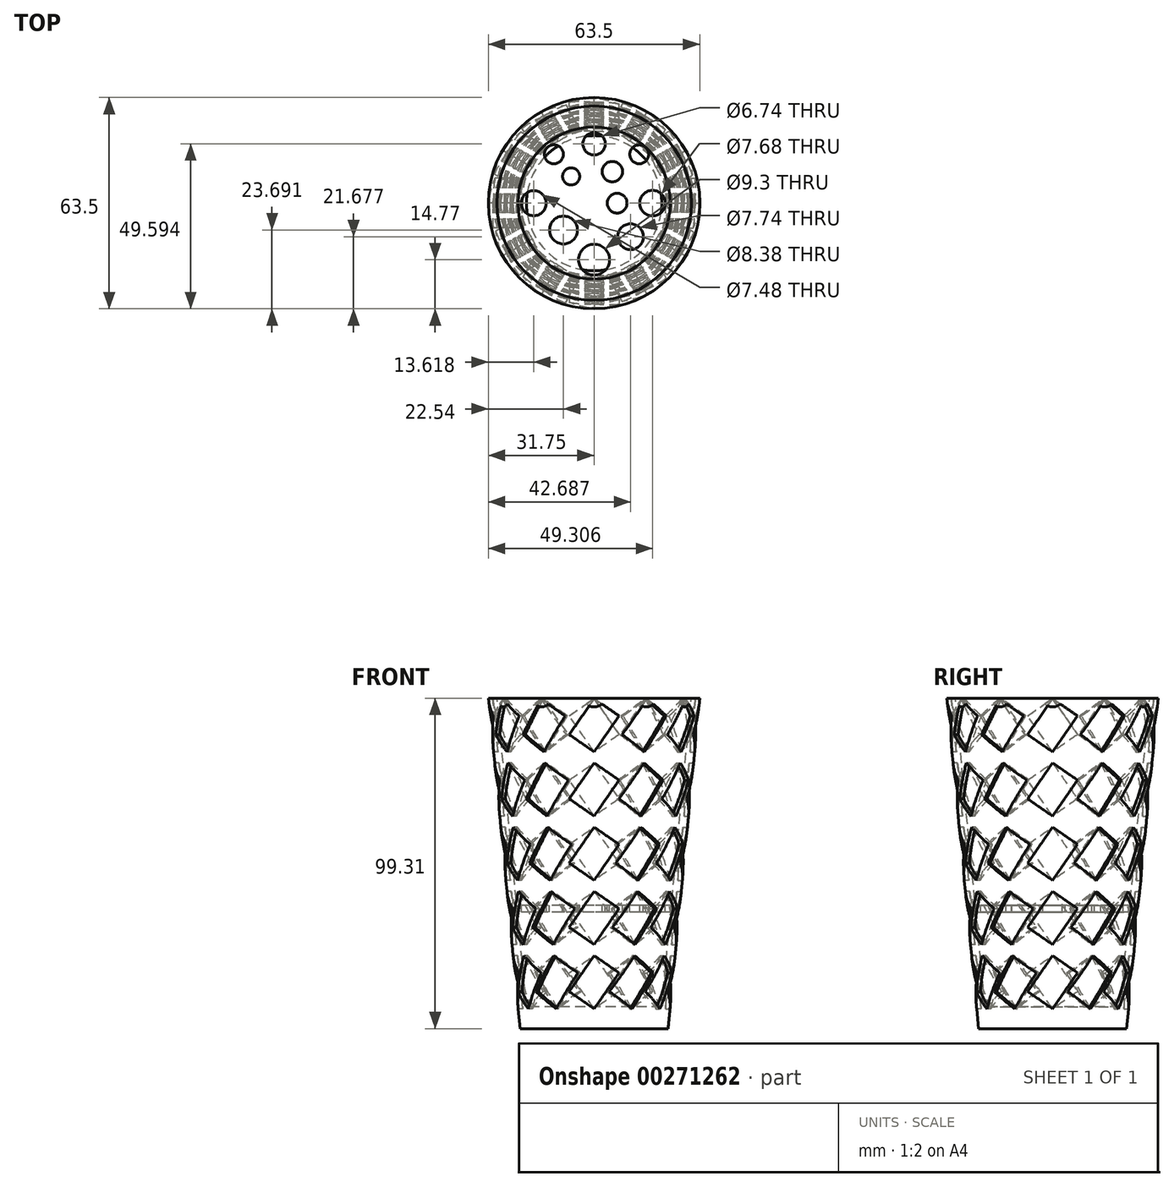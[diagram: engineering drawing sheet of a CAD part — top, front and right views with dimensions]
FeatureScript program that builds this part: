
annotation { "Feature Type Name" : "Feature", "Feature Type Description" : "" }
export const myFeature = defineFeature(function(context is Context, id is Id, definition is map)
    precondition{}
    {
        {
            var Q0;
            Q0=qCreatedBy(makeId("Top.planeOp"),FACE);
            cPlane(context, id + "F0", {"entities" : qUnion([Q0]), "cplaneType" : CPlaneType.OFFSET, "offset" : 50.8 * mm, "width" : 152.4 * mm, "height" : 152.4 * mm});
        }
        {
            var Q0;
            Q0=qCreatedBy(id+"F0.planeOp",FACE);
            var sketch = newSketch(context, id + "F1", { "sketchPlane" : qUnion([Q0])});
            skCircle(sketch, "E0", {"center": v(0, 0) * mm, "radius": 31.75 * mm});
            skSolve(sketch);
        }
        {
            var Q0;
            Q0=qCreatedBy(makeId("Top.planeOp"),FACE);
            cPlane(context, id + "F2", {"entities" : qUnion([Q0]), "cplaneType" : CPlaneType.OFFSET, "offset" : 48.5 * mm, "oppositeDirection" : true, "width" : 152.4 * mm, "height" : 152.4 * mm});
        }
        {
            var Q0;
            Q0=qCreatedBy(id+"F2.planeOp",FACE);
            var sketch = newSketch(context, id + "F3", { "sketchPlane" : qUnion([Q0])});
            skCircle(sketch, "E1", {"center": v(0, 0) * mm, "radius": 22.23 * mm});
            skSolve(sketch);
        }
        {
            var Q0;
            Q0=makeQuery(id+"F3.imprint","IMPRINT",FACE,{"disambiguationData":[TD([[makeQuery(id+"F3.imprint","IMPRINT",EDGE,{"derivedFrom":sQuery(id+"F3.wireOp",EDGE,"E1")}),1.0]])]});
            var Q1;
            Q1=makeQuery(id+"F1.imprint","IMPRINT",FACE,{"disambiguationData":[TD([[makeQuery(id+"F1.imprint","IMPRINT",EDGE,{"derivedFrom":sQuery(id+"F1.wireOp",EDGE,"E0")}),1.0]])]});
            loft(context, id + "F4", {"sheetProfilesArray" : [{ "sheetProfileEntities" : qUnion([Q0]) }, { "sheetProfileEntities" : qUnion([Q1]) }]});
        }
        {
            var Q0;
            Q0=qCreatedBy(makeId("Top.planeOp"),FACE);
            cPlane(context, id + "F5", {"entities" : qUnion([Q0]), "cplaneType" : CPlaneType.OFFSET, "offset" : 48.5 * mm, "oppositeDirection" : true, "width" : 152.4 * mm, "height" : 152.4 * mm});
        }
        {
            var Q0;
            Q0=qCreatedBy(id+"F5.planeOp",FACE);
            var sketch = newSketch(context, id + "F6", { "sketchPlane" : qUnion([Q0])});
            skCircle(sketch, "E2", {"center": v(0, 0) * mm, "radius": 22.23 * mm});
            skSolve(sketch);
        }
        {
            var Q0;
            Q0=makeQuery(id+"F4.opLoft","CAP_FACE",FACE,{"disambiguationData":[OSD([makeQuery(id+"F1.imprint","IMPRINT",FACE,{"disambiguationData":[TD([[makeQuery(id+"F1.imprint","IMPRINT",EDGE,{"derivedFrom":sQuery(id+"F1.wireOp",EDGE,"E0")}),1.0]])]})])],"isStart":true});
            var Q1;
            Q1=makeQuery(id+"F4.opLoft","CAP_FACE",FACE,{"disambiguationData":[OSD([makeQuery(id+"F3.imprint","IMPRINT",FACE,{"disambiguationData":[TD([[makeQuery(id+"F3.imprint","IMPRINT",EDGE,{"derivedFrom":sQuery(id+"F3.wireOp",EDGE,"E1")}),1.0]])]})])],"isStart":true});
            shell(context, id + "F7", {"entities" : qUnion([Q0, Q1]), "thickness" : 2.54 * mm});
        }
        {
            var Q0;
            Q0=makeQuery(id+"F6.imprint","IMPRINT",FACE,{"disambiguationData":[TD([[makeQuery(id+"F6.imprint","IMPRINT",EDGE,{"derivedFrom":sQuery(id+"F6.wireOp",EDGE,"E2")}),1.0]])]});
            extrude(context, id + "F8", {"entities" : qUnion([Q0]), "depth" : 6.35 * mm});
        }
        {
            var Q0;
            Q0=qCreatedBy(id+"F2.planeOp",FACE);
            cPlane(context, id + "F9", {"entities" : qUnion([Q0]), "cplaneType" : CPlaneType.OFFSET, "offset" : 35.05 * mm, "width" : 152.4 * mm, "height" : 152.4 * mm});
        }
        {
            var Q0;
            Q0=qCreatedBy(id+"F9.planeOp",FACE);
            var sketch = newSketch(context, id + "F10", { "sketchPlane" : qUnion([Q0])});
            skCircle(sketch, "E3", {"center": v(0, 0) * mm, "radius": 22.86 * mm});
            skSolve(sketch);
        }
        {
            var Q0;
            Q0=makeQuery(id+"F10.imprint","IMPRINT",FACE,{"disambiguationData":[TD([[makeQuery(id+"F10.imprint","IMPRINT",EDGE,{"derivedFrom":sQuery(id+"F10.wireOp",EDGE,"E3")}),1.0]])]});
            extrude(context, id + "F11", {"entities" : qUnion([Q0]), "depth" : 2.03 * mm});
        }
        {
            var Q0;
            Q0=makeQuery(id+"F11.opExtrude","CAP_FACE",FACE,{"disambiguationData":[OSD([sQuery(id+"F10.wireOp",EDGE,"E3")])],"isStart":false});
            var sketch = newSketch(context, id + "F12", { "sketchPlane" : qUnion([Q0])});
            skCircle(sketch, "E4", {"center": v(-12.09, 14.68) * mm, "radius": 2.85 * mm});
            skCircle(sketch, "E5", {"center": v(0, 17.84) * mm, "radius": 3.37 * mm});
            skCircle(sketch, "E6", {"center": v(13.53, 14.68) * mm, "radius": 2.83 * mm});
            skCircle(sketch, "E7", {"center": v(17.56, 0) * mm, "radius": 3.84 * mm});
            skCircle(sketch, "E8", {"center": v(0, -16.98) * mm, "radius": 4.65 * mm});
            skCircle(sketch, "E9", {"center": v(-18.13, 0) * mm, "radius": 3.74 * mm});
            skCircle(sketch, "E10", {"center": v(-9.2, -8.06) * mm, "radius": 4.2 * mm});
            skCircle(sketch, "E11", {"center": v(-6.9, 8.06) * mm, "radius": 2.57 * mm});
            skCircle(sketch, "E12", {"center": v(10.94, -10.07) * mm, "radius": 3.87 * mm});
            skCircle(sketch, "E13", {"center": v(5.47, 9.5) * mm, "radius": 3.06 * mm});
            skCircle(sketch, "E14", {"center": v(6.9, 0) * mm, "radius": 2.96 * mm});
            skSolve(sketch);
        }
        {
            var Q0;
            Q0 = qSketchRegion(id + "F12", true);
            extrude(context, id + "F13", {"entities" : qUnion([Q0]), "operationType" : NewBodyOperationType.REMOVE, "oppositeDirection" : true, "depth" : 4.06 * mm});
        }
        {
            var Q0;
            Q0=makeQuery(id+"F8.opExtrude","SWEPT_BODY",BODY,{"disambiguationData":[OSD([sQuery(id+"F6.wireOp",EDGE,"E2")])]});
            deleteBodies(context, id + "F14", {"entities" : qUnion([Q0])});
        }
        {
            var Q0;
            Q0=qCreatedBy(id+"F2.planeOp",FACE);
            var sketch = newSketch(context, id + "F15", { "sketchPlane" : qUnion([Q0])});
            skCircle(sketch, "E15", {"center": v(0, 0) * mm, "radius": 21.14 * mm});
            skSolve(sketch);
        }
        {
            var Q0;
            Q0=makeQuery(id+"F15.imprint","IMPRINT",FACE,{"disambiguationData":[TD([[makeQuery(id+"F15.imprint","IMPRINT",EDGE,{"derivedFrom":sQuery(id+"F15.wireOp",EDGE,"E15")}),1.0]])]});
            extrude(context, id + "F16", {"entities" : qUnion([Q0]), "operationType" : NewBodyOperationType.ADD, "depth" : 6.6 * mm});
        }
        {
            var Q0;
            Q0=makeQuery(id+"F16.boolean.opBoolean","MERGE",FACE,{"derivedFrom":[makeQuery(id+"F4.opLoft","CAP_FACE",FACE,{"disambiguationData":[OSD([makeQuery(id+"F3.imprint","IMPRINT",FACE,{"disambiguationData":[TD([[makeQuery(id+"F3.imprint","IMPRINT",EDGE,{"derivedFrom":sQuery(id+"F3.wireOp",EDGE,"E1")}),1.0]])]})])],"isStart":true}),makeQuery(id+"F16.opExtrude","CAP_FACE",FACE,{"disambiguationData":[OSD([sQuery(id+"F15.wireOp",EDGE,"E15")])],"isStart":true})]});
            var sketch = newSketch(context, id + "F17", { "sketchPlane" : qUnion([Q0])});
            skCircle(sketch, "E16", {"center": v(0, 0) * mm, "radius": 20.88 * mm});
            skSolve(sketch);
        }
        {
            var Q0;
            Q0=makeQuery(id+"F4.opLoft","CAP_FACE",FACE,{"disambiguationData":[OSD([makeQuery(id+"F1.imprint","IMPRINT",FACE,{"disambiguationData":[TD([[makeQuery(id+"F1.imprint","IMPRINT",EDGE,{"derivedFrom":sQuery(id+"F1.wireOp",EDGE,"E0")}),1.0]])]})])],"isStart":true});
            var sketch = newSketch(context, id + "F18", { "sketchPlane" : qUnion([Q0])});
            skCircle(sketch, "E17", {"center": v(0, 0) * mm, "radius": 30.42 * mm});
            skSolve(sketch);
        }
        {
            var Q0;
            Q0=makeQuery(id+"F18.imprint","IMPRINT",FACE,{"disambiguationData":[TD([[makeQuery(id+"F18.imprint","IMPRINT",EDGE,{"derivedFrom":sQuery(id+"F18.wireOp",EDGE,"E17")}),-1.0]])]});
            var Q1;
            Q1=sQuery(id+"F17.wireOp",EDGE,"E16");
            var Q2;
            Q2=sQuery(id+"F18.wireOp",EDGE,"E17");
            loft(context, id + "F19", {"bodyType" : ToolBodyType.SURFACE, "sheetProfilesArray" : [{ "sheetProfileEntities" : qUnion([Q0]) }], "wireProfilesArray" : [{ "wireProfileEntities" : qUnion([Q1]) }, { "wireProfileEntities" : qUnion([Q2]) }]});
        }
        {
            var Q0;
            Q0=qCreatedBy(makeId("Right.planeOp"),FACE);
            cPlane(context, id + "F20", {"entities" : qUnion([Q0]), "cplaneType" : CPlaneType.OFFSET, "offset" : 31.5 * mm, "width" : 152.4 * mm, "height" : 152.4 * mm});
        }
        {
            var Q0;
            Q0=qCreatedBy(id+"F20.planeOp",FACE);
            var sketch = newSketch(context, id + "F21", { "sketchPlane" : qUnion([Q0])});
            skLineSegment(sketch, "E18", {"start": v(0, 50.65) * mm, "end": v(7.48, 45.47) * mm});
            skLineSegment(sketch, "E19", {"start": v(7.48, 45.47) * mm, "end": v(0, 34.66) * mm});
            skLineSegment(sketch, "E20", {"start": v(0, 34.66) * mm, "end": v(-7.48, 39.85) * mm});
            skLineSegment(sketch, "E21", {"start": v(-7.48, 39.85) * mm, "end": v(0, 50.65) * mm});
            skLineSegment(sketch, "E22.0.1.0", {"start": v(0, 31.35) * mm, "end": v(7.48, 26.17) * mm});
            skLineSegment(sketch, "E22.0.1.1", {"start": v(7.48, 26.17) * mm, "end": v(0, 15.36) * mm});
            skLineSegment(sketch, "E22.0.1.2", {"start": v(0, 15.36) * mm, "end": v(-7.48, 20.54) * mm});
            skLineSegment(sketch, "E22.0.1.3", {"start": v(-7.48, 20.54) * mm, "end": v(0, 31.35) * mm});
            skLineSegment(sketch, "E22.0.2.0", {"start": v(0, 12.05) * mm, "end": v(7.48, 6.87) * mm});
            skLineSegment(sketch, "E22.0.2.1", {"start": v(7.48, 6.87) * mm, "end": v(0, -3.94) * mm});
            skLineSegment(sketch, "E22.0.2.2", {"start": v(0, -3.94) * mm, "end": v(-7.48, 1.24) * mm});
            skLineSegment(sketch, "E22.0.2.3", {"start": v(-7.48, 1.24) * mm, "end": v(0, 12.05) * mm});
            skLineSegment(sketch, "E22.0.3.0", {"start": v(0, -7.26) * mm, "end": v(7.48, -12.44) * mm});
            skLineSegment(sketch, "E22.0.3.1", {"start": v(7.48, -12.44) * mm, "end": v(0, -23.25) * mm});
            skLineSegment(sketch, "E22.0.3.2", {"start": v(0, -23.25) * mm, "end": v(-7.48, -18.07) * mm});
            skLineSegment(sketch, "E22.0.3.3", {"start": v(-7.48, -18.07) * mm, "end": v(0, -7.26) * mm});
            skLineSegment(sketch, "E22.0.4.0", {"start": v(0, -26.56) * mm, "end": v(7.48, -31.74) * mm});
            skLineSegment(sketch, "E22.0.4.1", {"start": v(7.48, -31.74) * mm, "end": v(0, -42.55) * mm});
            skLineSegment(sketch, "E22.0.4.2", {"start": v(0, -42.55) * mm, "end": v(-7.48, -37.37) * mm});
            skLineSegment(sketch, "E22.0.4.3", {"start": v(-7.48, -37.37) * mm, "end": v(0, -26.56) * mm});
            skLineSegment(sketch, "E22.direction1", {"start": v(-7.48, 39.85) * mm, "end": v(17.92, 39.85) * mm, "construction": true});
            skLineSegment(sketch, "E22.direction2", {"start": v(-7.48, 39.85) * mm, "end": v(-7.48, 20.54) * mm, "construction": true});
            skSolve(sketch);
        }
        {
            var Q0;
            Q0 = qSketchRegion(id + "F21", true);
            var Q1;
            Q1=makeQuery(id+"F19.opLoft","SWEPT_BODY",BODY,{"disambiguationData":[OSD([sQuery(id+"F17.wireOp",EDGE,"E16"),sQuery(id+"F18.wireOp",EDGE,"E17")])]});
            extrude(context, id + "F22", {"entities" : qUnion([Q0]), "endBound" : BoundingType.UP_TO_BODY, "oppositeDirection" : true, "endBoundEntityBody" : qUnion([Q1]), "depth" : 2.54 * mm});
        }
        {
            var Q0;
            Q0=qCreatedBy(makeId("Front.planeOp"),FACE);
            var sketch = newSketch(context, id + "F23", { "sketchPlane" : qUnion([Q0])});
            skLineSegment(sketch, "E23", {"start": v(0, -61.6) * mm, "end": v(0, 66.06) * mm, "construction": true});
            skSolve(sketch);
        }
        {
            var Q0;
            Q0=makeQuery(id+"F22.opExtrude","SWEPT_BODY",BODY,{"disambiguationData":[OSD([sQuery(id+"F21.wireOp",EDGE,"E18"),sQuery(id+"F21.wireOp",EDGE,"E19"),sQuery(id+"F21.wireOp",EDGE,"E20"),sQuery(id+"F21.wireOp",EDGE,"E21")])]});
            var Q1;
            Q1=makeQuery(id+"F22.opExtrude","SWEPT_BODY",BODY,{"disambiguationData":[OSD([sQuery(id+"F21.wireOp",EDGE,"E22.0.1.0"),sQuery(id+"F21.wireOp",EDGE,"E22.0.1.1"),sQuery(id+"F21.wireOp",EDGE,"E22.0.1.2"),sQuery(id+"F21.wireOp",EDGE,"E22.0.1.3")])]});
            var Q2;
            Q2=makeQuery(id+"F22.opExtrude","SWEPT_BODY",BODY,{"disambiguationData":[OSD([sQuery(id+"F21.wireOp",EDGE,"E22.0.2.0"),sQuery(id+"F21.wireOp",EDGE,"E22.0.2.1"),sQuery(id+"F21.wireOp",EDGE,"E22.0.2.2"),sQuery(id+"F21.wireOp",EDGE,"E22.0.2.3")])]});
            var Q3;
            Q3=makeQuery(id+"F22.opExtrude","SWEPT_BODY",BODY,{"disambiguationData":[OSD([sQuery(id+"F21.wireOp",EDGE,"E22.0.3.0"),sQuery(id+"F21.wireOp",EDGE,"E22.0.3.1"),sQuery(id+"F21.wireOp",EDGE,"E22.0.3.2"),sQuery(id+"F21.wireOp",EDGE,"E22.0.3.3")])]});
            var Q4;
            Q4=makeQuery(id+"F22.opExtrude","SWEPT_BODY",BODY,{"disambiguationData":[OSD([sQuery(id+"F21.wireOp",EDGE,"E22.0.4.0"),sQuery(id+"F21.wireOp",EDGE,"E22.0.4.1"),sQuery(id+"F21.wireOp",EDGE,"E22.0.4.2"),sQuery(id+"F21.wireOp",EDGE,"E22.0.4.3")])]});
            var Q5;
            Q5=sQuery(id+"F23.wireOp",EDGE,"E23");
            circularPattern(context, id + "F24", {"entities" : qUnion([Q0, Q1, Q2, Q3, Q4]), "axis" : qUnion([Q5]), "angle" : 360 * degree, "instanceCount" : 12, "equalSpace" : true});
        }
        {
            var Q0;
            Q0=makeQuery(id+"F24.opPattern","COPY",BODY,{"derivedFrom":makeQuery(id+"F22.opExtrude","SWEPT_BODY",BODY,{"disambiguationData":[OSD([sQuery(id+"F21.wireOp",EDGE,"E22.0.4.0"),sQuery(id+"F21.wireOp",EDGE,"E22.0.4.1"),sQuery(id+"F21.wireOp",EDGE,"E22.0.4.2"),sQuery(id+"F21.wireOp",EDGE,"E22.0.4.3")])]}),"instanceName":"11"});
            var Q1;
            Q1=makeQuery(id+"F22.opExtrude","SWEPT_BODY",BODY,{"disambiguationData":[OSD([sQuery(id+"F21.wireOp",EDGE,"E18"),sQuery(id+"F21.wireOp",EDGE,"E19"),sQuery(id+"F21.wireOp",EDGE,"E20"),sQuery(id+"F21.wireOp",EDGE,"E21")])]});
            var Q2;
            Q2=makeQuery(id+"F22.opExtrude","SWEPT_BODY",BODY,{"disambiguationData":[OSD([sQuery(id+"F21.wireOp",EDGE,"E22.0.1.0"),sQuery(id+"F21.wireOp",EDGE,"E22.0.1.1"),sQuery(id+"F21.wireOp",EDGE,"E22.0.1.2"),sQuery(id+"F21.wireOp",EDGE,"E22.0.1.3")])]});
            var Q3;
            Q3=makeQuery(id+"F22.opExtrude","SWEPT_BODY",BODY,{"disambiguationData":[OSD([sQuery(id+"F21.wireOp",EDGE,"E22.0.2.0"),sQuery(id+"F21.wireOp",EDGE,"E22.0.2.1"),sQuery(id+"F21.wireOp",EDGE,"E22.0.2.2"),sQuery(id+"F21.wireOp",EDGE,"E22.0.2.3")])]});
            var Q4;
            Q4=makeQuery(id+"F22.opExtrude","SWEPT_BODY",BODY,{"disambiguationData":[OSD([sQuery(id+"F21.wireOp",EDGE,"E22.0.3.0"),sQuery(id+"F21.wireOp",EDGE,"E22.0.3.1"),sQuery(id+"F21.wireOp",EDGE,"E22.0.3.2"),sQuery(id+"F21.wireOp",EDGE,"E22.0.3.3")])]});
            var Q5;
            Q5=makeQuery(id+"F22.opExtrude","SWEPT_BODY",BODY,{"disambiguationData":[OSD([sQuery(id+"F21.wireOp",EDGE,"E22.0.4.0"),sQuery(id+"F21.wireOp",EDGE,"E22.0.4.1"),sQuery(id+"F21.wireOp",EDGE,"E22.0.4.2"),sQuery(id+"F21.wireOp",EDGE,"E22.0.4.3")])]});
            var Q6;
            Q6=makeQuery(id+"F24.opPattern","COPY",BODY,{"derivedFrom":makeQuery(id+"F22.opExtrude","SWEPT_BODY",BODY,{"disambiguationData":[OSD([sQuery(id+"F21.wireOp",EDGE,"E18"),sQuery(id+"F21.wireOp",EDGE,"E19"),sQuery(id+"F21.wireOp",EDGE,"E20"),sQuery(id+"F21.wireOp",EDGE,"E21")])]}),"instanceName":"1"});
            var Q7;
            Q7=makeQuery(id+"F24.opPattern","COPY",BODY,{"derivedFrom":makeQuery(id+"F22.opExtrude","SWEPT_BODY",BODY,{"disambiguationData":[OSD([sQuery(id+"F21.wireOp",EDGE,"E22.0.1.0"),sQuery(id+"F21.wireOp",EDGE,"E22.0.1.1"),sQuery(id+"F21.wireOp",EDGE,"E22.0.1.2"),sQuery(id+"F21.wireOp",EDGE,"E22.0.1.3")])]}),"instanceName":"1"});
            var Q8;
            Q8=makeQuery(id+"F24.opPattern","COPY",BODY,{"derivedFrom":makeQuery(id+"F22.opExtrude","SWEPT_BODY",BODY,{"disambiguationData":[OSD([sQuery(id+"F21.wireOp",EDGE,"E22.0.2.0"),sQuery(id+"F21.wireOp",EDGE,"E22.0.2.1"),sQuery(id+"F21.wireOp",EDGE,"E22.0.2.2"),sQuery(id+"F21.wireOp",EDGE,"E22.0.2.3")])]}),"instanceName":"1"});
            var Q9;
            Q9=makeQuery(id+"F24.opPattern","COPY",BODY,{"derivedFrom":makeQuery(id+"F22.opExtrude","SWEPT_BODY",BODY,{"disambiguationData":[OSD([sQuery(id+"F21.wireOp",EDGE,"E22.0.3.0"),sQuery(id+"F21.wireOp",EDGE,"E22.0.3.1"),sQuery(id+"F21.wireOp",EDGE,"E22.0.3.2"),sQuery(id+"F21.wireOp",EDGE,"E22.0.3.3")])]}),"instanceName":"1"});
            var Q10;
            Q10=makeQuery(id+"F24.opPattern","COPY",BODY,{"derivedFrom":makeQuery(id+"F22.opExtrude","SWEPT_BODY",BODY,{"disambiguationData":[OSD([sQuery(id+"F21.wireOp",EDGE,"E22.0.4.0"),sQuery(id+"F21.wireOp",EDGE,"E22.0.4.1"),sQuery(id+"F21.wireOp",EDGE,"E22.0.4.2"),sQuery(id+"F21.wireOp",EDGE,"E22.0.4.3")])]}),"instanceName":"1"});
            var Q11;
            Q11=makeQuery(id+"F24.opPattern","COPY",BODY,{"derivedFrom":makeQuery(id+"F22.opExtrude","SWEPT_BODY",BODY,{"disambiguationData":[OSD([sQuery(id+"F21.wireOp",EDGE,"E18"),sQuery(id+"F21.wireOp",EDGE,"E19"),sQuery(id+"F21.wireOp",EDGE,"E20"),sQuery(id+"F21.wireOp",EDGE,"E21")])]}),"instanceName":"2"});
            var Q12;
            Q12=makeQuery(id+"F24.opPattern","COPY",BODY,{"derivedFrom":makeQuery(id+"F22.opExtrude","SWEPT_BODY",BODY,{"disambiguationData":[OSD([sQuery(id+"F21.wireOp",EDGE,"E22.0.1.0"),sQuery(id+"F21.wireOp",EDGE,"E22.0.1.1"),sQuery(id+"F21.wireOp",EDGE,"E22.0.1.2"),sQuery(id+"F21.wireOp",EDGE,"E22.0.1.3")])]}),"instanceName":"2"});
            var Q13;
            Q13=makeQuery(id+"F24.opPattern","COPY",BODY,{"derivedFrom":makeQuery(id+"F22.opExtrude","SWEPT_BODY",BODY,{"disambiguationData":[OSD([sQuery(id+"F21.wireOp",EDGE,"E22.0.2.0"),sQuery(id+"F21.wireOp",EDGE,"E22.0.2.1"),sQuery(id+"F21.wireOp",EDGE,"E22.0.2.2"),sQuery(id+"F21.wireOp",EDGE,"E22.0.2.3")])]}),"instanceName":"2"});
            var Q14;
            Q14=makeQuery(id+"F24.opPattern","COPY",BODY,{"derivedFrom":makeQuery(id+"F22.opExtrude","SWEPT_BODY",BODY,{"disambiguationData":[OSD([sQuery(id+"F21.wireOp",EDGE,"E22.0.3.0"),sQuery(id+"F21.wireOp",EDGE,"E22.0.3.1"),sQuery(id+"F21.wireOp",EDGE,"E22.0.3.2"),sQuery(id+"F21.wireOp",EDGE,"E22.0.3.3")])]}),"instanceName":"2"});
            var Q15;
            Q15=makeQuery(id+"F24.opPattern","COPY",BODY,{"derivedFrom":makeQuery(id+"F22.opExtrude","SWEPT_BODY",BODY,{"disambiguationData":[OSD([sQuery(id+"F21.wireOp",EDGE,"E22.0.4.0"),sQuery(id+"F21.wireOp",EDGE,"E22.0.4.1"),sQuery(id+"F21.wireOp",EDGE,"E22.0.4.2"),sQuery(id+"F21.wireOp",EDGE,"E22.0.4.3")])]}),"instanceName":"2"});
            var Q16;
            Q16=makeQuery(id+"F24.opPattern","COPY",BODY,{"derivedFrom":makeQuery(id+"F22.opExtrude","SWEPT_BODY",BODY,{"disambiguationData":[OSD([sQuery(id+"F21.wireOp",EDGE,"E18"),sQuery(id+"F21.wireOp",EDGE,"E19"),sQuery(id+"F21.wireOp",EDGE,"E20"),sQuery(id+"F21.wireOp",EDGE,"E21")])]}),"instanceName":"3"});
            var Q17;
            Q17=makeQuery(id+"F24.opPattern","COPY",BODY,{"derivedFrom":makeQuery(id+"F22.opExtrude","SWEPT_BODY",BODY,{"disambiguationData":[OSD([sQuery(id+"F21.wireOp",EDGE,"E22.0.1.0"),sQuery(id+"F21.wireOp",EDGE,"E22.0.1.1"),sQuery(id+"F21.wireOp",EDGE,"E22.0.1.2"),sQuery(id+"F21.wireOp",EDGE,"E22.0.1.3")])]}),"instanceName":"3"});
            var Q18;
            Q18=makeQuery(id+"F24.opPattern","COPY",BODY,{"derivedFrom":makeQuery(id+"F22.opExtrude","SWEPT_BODY",BODY,{"disambiguationData":[OSD([sQuery(id+"F21.wireOp",EDGE,"E22.0.2.0"),sQuery(id+"F21.wireOp",EDGE,"E22.0.2.1"),sQuery(id+"F21.wireOp",EDGE,"E22.0.2.2"),sQuery(id+"F21.wireOp",EDGE,"E22.0.2.3")])]}),"instanceName":"3"});
            var Q19;
            Q19=makeQuery(id+"F24.opPattern","COPY",BODY,{"derivedFrom":makeQuery(id+"F22.opExtrude","SWEPT_BODY",BODY,{"disambiguationData":[OSD([sQuery(id+"F21.wireOp",EDGE,"E22.0.3.0"),sQuery(id+"F21.wireOp",EDGE,"E22.0.3.1"),sQuery(id+"F21.wireOp",EDGE,"E22.0.3.2"),sQuery(id+"F21.wireOp",EDGE,"E22.0.3.3")])]}),"instanceName":"3"});
            var Q20;
            Q20=makeQuery(id+"F24.opPattern","COPY",BODY,{"derivedFrom":makeQuery(id+"F22.opExtrude","SWEPT_BODY",BODY,{"disambiguationData":[OSD([sQuery(id+"F21.wireOp",EDGE,"E22.0.4.0"),sQuery(id+"F21.wireOp",EDGE,"E22.0.4.1"),sQuery(id+"F21.wireOp",EDGE,"E22.0.4.2"),sQuery(id+"F21.wireOp",EDGE,"E22.0.4.3")])]}),"instanceName":"3"});
            var Q21;
            Q21=makeQuery(id+"F24.opPattern","COPY",BODY,{"derivedFrom":makeQuery(id+"F22.opExtrude","SWEPT_BODY",BODY,{"disambiguationData":[OSD([sQuery(id+"F21.wireOp",EDGE,"E18"),sQuery(id+"F21.wireOp",EDGE,"E19"),sQuery(id+"F21.wireOp",EDGE,"E20"),sQuery(id+"F21.wireOp",EDGE,"E21")])]}),"instanceName":"4"});
            var Q22;
            Q22=makeQuery(id+"F24.opPattern","COPY",BODY,{"derivedFrom":makeQuery(id+"F22.opExtrude","SWEPT_BODY",BODY,{"disambiguationData":[OSD([sQuery(id+"F21.wireOp",EDGE,"E22.0.1.0"),sQuery(id+"F21.wireOp",EDGE,"E22.0.1.1"),sQuery(id+"F21.wireOp",EDGE,"E22.0.1.2"),sQuery(id+"F21.wireOp",EDGE,"E22.0.1.3")])]}),"instanceName":"4"});
            var Q23;
            Q23=makeQuery(id+"F24.opPattern","COPY",BODY,{"derivedFrom":makeQuery(id+"F22.opExtrude","SWEPT_BODY",BODY,{"disambiguationData":[OSD([sQuery(id+"F21.wireOp",EDGE,"E22.0.2.0"),sQuery(id+"F21.wireOp",EDGE,"E22.0.2.1"),sQuery(id+"F21.wireOp",EDGE,"E22.0.2.2"),sQuery(id+"F21.wireOp",EDGE,"E22.0.2.3")])]}),"instanceName":"4"});
            var Q24;
            Q24=makeQuery(id+"F24.opPattern","COPY",BODY,{"derivedFrom":makeQuery(id+"F22.opExtrude","SWEPT_BODY",BODY,{"disambiguationData":[OSD([sQuery(id+"F21.wireOp",EDGE,"E22.0.3.0"),sQuery(id+"F21.wireOp",EDGE,"E22.0.3.1"),sQuery(id+"F21.wireOp",EDGE,"E22.0.3.2"),sQuery(id+"F21.wireOp",EDGE,"E22.0.3.3")])]}),"instanceName":"4"});
            var Q25;
            Q25=makeQuery(id+"F24.opPattern","COPY",BODY,{"derivedFrom":makeQuery(id+"F22.opExtrude","SWEPT_BODY",BODY,{"disambiguationData":[OSD([sQuery(id+"F21.wireOp",EDGE,"E22.0.4.0"),sQuery(id+"F21.wireOp",EDGE,"E22.0.4.1"),sQuery(id+"F21.wireOp",EDGE,"E22.0.4.2"),sQuery(id+"F21.wireOp",EDGE,"E22.0.4.3")])]}),"instanceName":"4"});
            var Q26;
            Q26=makeQuery(id+"F24.opPattern","COPY",BODY,{"derivedFrom":makeQuery(id+"F22.opExtrude","SWEPT_BODY",BODY,{"disambiguationData":[OSD([sQuery(id+"F21.wireOp",EDGE,"E18"),sQuery(id+"F21.wireOp",EDGE,"E19"),sQuery(id+"F21.wireOp",EDGE,"E20"),sQuery(id+"F21.wireOp",EDGE,"E21")])]}),"instanceName":"5"});
            var Q27;
            Q27=makeQuery(id+"F24.opPattern","COPY",BODY,{"derivedFrom":makeQuery(id+"F22.opExtrude","SWEPT_BODY",BODY,{"disambiguationData":[OSD([sQuery(id+"F21.wireOp",EDGE,"E22.0.1.0"),sQuery(id+"F21.wireOp",EDGE,"E22.0.1.1"),sQuery(id+"F21.wireOp",EDGE,"E22.0.1.2"),sQuery(id+"F21.wireOp",EDGE,"E22.0.1.3")])]}),"instanceName":"5"});
            var Q28;
            Q28=makeQuery(id+"F24.opPattern","COPY",BODY,{"derivedFrom":makeQuery(id+"F22.opExtrude","SWEPT_BODY",BODY,{"disambiguationData":[OSD([sQuery(id+"F21.wireOp",EDGE,"E22.0.2.0"),sQuery(id+"F21.wireOp",EDGE,"E22.0.2.1"),sQuery(id+"F21.wireOp",EDGE,"E22.0.2.2"),sQuery(id+"F21.wireOp",EDGE,"E22.0.2.3")])]}),"instanceName":"5"});
            var Q29;
            Q29=makeQuery(id+"F24.opPattern","COPY",BODY,{"derivedFrom":makeQuery(id+"F22.opExtrude","SWEPT_BODY",BODY,{"disambiguationData":[OSD([sQuery(id+"F21.wireOp",EDGE,"E22.0.3.0"),sQuery(id+"F21.wireOp",EDGE,"E22.0.3.1"),sQuery(id+"F21.wireOp",EDGE,"E22.0.3.2"),sQuery(id+"F21.wireOp",EDGE,"E22.0.3.3")])]}),"instanceName":"5"});
            var Q30;
            Q30=makeQuery(id+"F24.opPattern","COPY",BODY,{"derivedFrom":makeQuery(id+"F22.opExtrude","SWEPT_BODY",BODY,{"disambiguationData":[OSD([sQuery(id+"F21.wireOp",EDGE,"E22.0.4.0"),sQuery(id+"F21.wireOp",EDGE,"E22.0.4.1"),sQuery(id+"F21.wireOp",EDGE,"E22.0.4.2"),sQuery(id+"F21.wireOp",EDGE,"E22.0.4.3")])]}),"instanceName":"5"});
            var Q31;
            Q31=makeQuery(id+"F24.opPattern","COPY",BODY,{"derivedFrom":makeQuery(id+"F22.opExtrude","SWEPT_BODY",BODY,{"disambiguationData":[OSD([sQuery(id+"F21.wireOp",EDGE,"E18"),sQuery(id+"F21.wireOp",EDGE,"E19"),sQuery(id+"F21.wireOp",EDGE,"E20"),sQuery(id+"F21.wireOp",EDGE,"E21")])]}),"instanceName":"6"});
            var Q32;
            Q32=makeQuery(id+"F24.opPattern","COPY",BODY,{"derivedFrom":makeQuery(id+"F22.opExtrude","SWEPT_BODY",BODY,{"disambiguationData":[OSD([sQuery(id+"F21.wireOp",EDGE,"E22.0.1.0"),sQuery(id+"F21.wireOp",EDGE,"E22.0.1.1"),sQuery(id+"F21.wireOp",EDGE,"E22.0.1.2"),sQuery(id+"F21.wireOp",EDGE,"E22.0.1.3")])]}),"instanceName":"6"});
            var Q33;
            Q33=makeQuery(id+"F24.opPattern","COPY",BODY,{"derivedFrom":makeQuery(id+"F22.opExtrude","SWEPT_BODY",BODY,{"disambiguationData":[OSD([sQuery(id+"F21.wireOp",EDGE,"E22.0.2.0"),sQuery(id+"F21.wireOp",EDGE,"E22.0.2.1"),sQuery(id+"F21.wireOp",EDGE,"E22.0.2.2"),sQuery(id+"F21.wireOp",EDGE,"E22.0.2.3")])]}),"instanceName":"6"});
            var Q34;
            Q34=makeQuery(id+"F24.opPattern","COPY",BODY,{"derivedFrom":makeQuery(id+"F22.opExtrude","SWEPT_BODY",BODY,{"disambiguationData":[OSD([sQuery(id+"F21.wireOp",EDGE,"E22.0.3.0"),sQuery(id+"F21.wireOp",EDGE,"E22.0.3.1"),sQuery(id+"F21.wireOp",EDGE,"E22.0.3.2"),sQuery(id+"F21.wireOp",EDGE,"E22.0.3.3")])]}),"instanceName":"6"});
            var Q35;
            Q35=makeQuery(id+"F24.opPattern","COPY",BODY,{"derivedFrom":makeQuery(id+"F22.opExtrude","SWEPT_BODY",BODY,{"disambiguationData":[OSD([sQuery(id+"F21.wireOp",EDGE,"E22.0.4.0"),sQuery(id+"F21.wireOp",EDGE,"E22.0.4.1"),sQuery(id+"F21.wireOp",EDGE,"E22.0.4.2"),sQuery(id+"F21.wireOp",EDGE,"E22.0.4.3")])]}),"instanceName":"6"});
            var Q36;
            Q36=makeQuery(id+"F24.opPattern","COPY",BODY,{"derivedFrom":makeQuery(id+"F22.opExtrude","SWEPT_BODY",BODY,{"disambiguationData":[OSD([sQuery(id+"F21.wireOp",EDGE,"E18"),sQuery(id+"F21.wireOp",EDGE,"E19"),sQuery(id+"F21.wireOp",EDGE,"E20"),sQuery(id+"F21.wireOp",EDGE,"E21")])]}),"instanceName":"7"});
            var Q37;
            Q37=makeQuery(id+"F24.opPattern","COPY",BODY,{"derivedFrom":makeQuery(id+"F22.opExtrude","SWEPT_BODY",BODY,{"disambiguationData":[OSD([sQuery(id+"F21.wireOp",EDGE,"E22.0.1.0"),sQuery(id+"F21.wireOp",EDGE,"E22.0.1.1"),sQuery(id+"F21.wireOp",EDGE,"E22.0.1.2"),sQuery(id+"F21.wireOp",EDGE,"E22.0.1.3")])]}),"instanceName":"7"});
            var Q38;
            Q38=makeQuery(id+"F24.opPattern","COPY",BODY,{"derivedFrom":makeQuery(id+"F22.opExtrude","SWEPT_BODY",BODY,{"disambiguationData":[OSD([sQuery(id+"F21.wireOp",EDGE,"E22.0.2.0"),sQuery(id+"F21.wireOp",EDGE,"E22.0.2.1"),sQuery(id+"F21.wireOp",EDGE,"E22.0.2.2"),sQuery(id+"F21.wireOp",EDGE,"E22.0.2.3")])]}),"instanceName":"7"});
            var Q39;
            Q39=makeQuery(id+"F24.opPattern","COPY",BODY,{"derivedFrom":makeQuery(id+"F22.opExtrude","SWEPT_BODY",BODY,{"disambiguationData":[OSD([sQuery(id+"F21.wireOp",EDGE,"E22.0.3.0"),sQuery(id+"F21.wireOp",EDGE,"E22.0.3.1"),sQuery(id+"F21.wireOp",EDGE,"E22.0.3.2"),sQuery(id+"F21.wireOp",EDGE,"E22.0.3.3")])]}),"instanceName":"7"});
            var Q40;
            Q40=makeQuery(id+"F24.opPattern","COPY",BODY,{"derivedFrom":makeQuery(id+"F22.opExtrude","SWEPT_BODY",BODY,{"disambiguationData":[OSD([sQuery(id+"F21.wireOp",EDGE,"E22.0.4.0"),sQuery(id+"F21.wireOp",EDGE,"E22.0.4.1"),sQuery(id+"F21.wireOp",EDGE,"E22.0.4.2"),sQuery(id+"F21.wireOp",EDGE,"E22.0.4.3")])]}),"instanceName":"7"});
            var Q41;
            Q41=makeQuery(id+"F24.opPattern","COPY",BODY,{"derivedFrom":makeQuery(id+"F22.opExtrude","SWEPT_BODY",BODY,{"disambiguationData":[OSD([sQuery(id+"F21.wireOp",EDGE,"E18"),sQuery(id+"F21.wireOp",EDGE,"E19"),sQuery(id+"F21.wireOp",EDGE,"E20"),sQuery(id+"F21.wireOp",EDGE,"E21")])]}),"instanceName":"8"});
            var Q42;
            Q42=makeQuery(id+"F24.opPattern","COPY",BODY,{"derivedFrom":makeQuery(id+"F22.opExtrude","SWEPT_BODY",BODY,{"disambiguationData":[OSD([sQuery(id+"F21.wireOp",EDGE,"E22.0.1.0"),sQuery(id+"F21.wireOp",EDGE,"E22.0.1.1"),sQuery(id+"F21.wireOp",EDGE,"E22.0.1.2"),sQuery(id+"F21.wireOp",EDGE,"E22.0.1.3")])]}),"instanceName":"8"});
            var Q43;
            Q43=makeQuery(id+"F24.opPattern","COPY",BODY,{"derivedFrom":makeQuery(id+"F22.opExtrude","SWEPT_BODY",BODY,{"disambiguationData":[OSD([sQuery(id+"F21.wireOp",EDGE,"E22.0.2.0"),sQuery(id+"F21.wireOp",EDGE,"E22.0.2.1"),sQuery(id+"F21.wireOp",EDGE,"E22.0.2.2"),sQuery(id+"F21.wireOp",EDGE,"E22.0.2.3")])]}),"instanceName":"8"});
            var Q44;
            Q44=makeQuery(id+"F24.opPattern","COPY",BODY,{"derivedFrom":makeQuery(id+"F22.opExtrude","SWEPT_BODY",BODY,{"disambiguationData":[OSD([sQuery(id+"F21.wireOp",EDGE,"E22.0.3.0"),sQuery(id+"F21.wireOp",EDGE,"E22.0.3.1"),sQuery(id+"F21.wireOp",EDGE,"E22.0.3.2"),sQuery(id+"F21.wireOp",EDGE,"E22.0.3.3")])]}),"instanceName":"8"});
            var Q45;
            Q45=makeQuery(id+"F24.opPattern","COPY",BODY,{"derivedFrom":makeQuery(id+"F22.opExtrude","SWEPT_BODY",BODY,{"disambiguationData":[OSD([sQuery(id+"F21.wireOp",EDGE,"E22.0.4.0"),sQuery(id+"F21.wireOp",EDGE,"E22.0.4.1"),sQuery(id+"F21.wireOp",EDGE,"E22.0.4.2"),sQuery(id+"F21.wireOp",EDGE,"E22.0.4.3")])]}),"instanceName":"8"});
            var Q46;
            Q46=makeQuery(id+"F24.opPattern","COPY",BODY,{"derivedFrom":makeQuery(id+"F22.opExtrude","SWEPT_BODY",BODY,{"disambiguationData":[OSD([sQuery(id+"F21.wireOp",EDGE,"E18"),sQuery(id+"F21.wireOp",EDGE,"E19"),sQuery(id+"F21.wireOp",EDGE,"E20"),sQuery(id+"F21.wireOp",EDGE,"E21")])]}),"instanceName":"9"});
            var Q47;
            Q47=makeQuery(id+"F24.opPattern","COPY",BODY,{"derivedFrom":makeQuery(id+"F22.opExtrude","SWEPT_BODY",BODY,{"disambiguationData":[OSD([sQuery(id+"F21.wireOp",EDGE,"E22.0.1.0"),sQuery(id+"F21.wireOp",EDGE,"E22.0.1.1"),sQuery(id+"F21.wireOp",EDGE,"E22.0.1.2"),sQuery(id+"F21.wireOp",EDGE,"E22.0.1.3")])]}),"instanceName":"9"});
            var Q48;
            Q48=makeQuery(id+"F24.opPattern","COPY",BODY,{"derivedFrom":makeQuery(id+"F22.opExtrude","SWEPT_BODY",BODY,{"disambiguationData":[OSD([sQuery(id+"F21.wireOp",EDGE,"E22.0.2.0"),sQuery(id+"F21.wireOp",EDGE,"E22.0.2.1"),sQuery(id+"F21.wireOp",EDGE,"E22.0.2.2"),sQuery(id+"F21.wireOp",EDGE,"E22.0.2.3")])]}),"instanceName":"9"});
            var Q49;
            Q49=makeQuery(id+"F24.opPattern","COPY",BODY,{"derivedFrom":makeQuery(id+"F22.opExtrude","SWEPT_BODY",BODY,{"disambiguationData":[OSD([sQuery(id+"F21.wireOp",EDGE,"E22.0.3.0"),sQuery(id+"F21.wireOp",EDGE,"E22.0.3.1"),sQuery(id+"F21.wireOp",EDGE,"E22.0.3.2"),sQuery(id+"F21.wireOp",EDGE,"E22.0.3.3")])]}),"instanceName":"9"});
            var Q50;
            Q50=makeQuery(id+"F24.opPattern","COPY",BODY,{"derivedFrom":makeQuery(id+"F22.opExtrude","SWEPT_BODY",BODY,{"disambiguationData":[OSD([sQuery(id+"F21.wireOp",EDGE,"E22.0.4.0"),sQuery(id+"F21.wireOp",EDGE,"E22.0.4.1"),sQuery(id+"F21.wireOp",EDGE,"E22.0.4.2"),sQuery(id+"F21.wireOp",EDGE,"E22.0.4.3")])]}),"instanceName":"9"});
            var Q51;
            Q51=makeQuery(id+"F24.opPattern","COPY",BODY,{"derivedFrom":makeQuery(id+"F22.opExtrude","SWEPT_BODY",BODY,{"disambiguationData":[OSD([sQuery(id+"F21.wireOp",EDGE,"E18"),sQuery(id+"F21.wireOp",EDGE,"E19"),sQuery(id+"F21.wireOp",EDGE,"E20"),sQuery(id+"F21.wireOp",EDGE,"E21")])]}),"instanceName":"10"});
            var Q52;
            Q52=makeQuery(id+"F24.opPattern","COPY",BODY,{"derivedFrom":makeQuery(id+"F22.opExtrude","SWEPT_BODY",BODY,{"disambiguationData":[OSD([sQuery(id+"F21.wireOp",EDGE,"E22.0.1.0"),sQuery(id+"F21.wireOp",EDGE,"E22.0.1.1"),sQuery(id+"F21.wireOp",EDGE,"E22.0.1.2"),sQuery(id+"F21.wireOp",EDGE,"E22.0.1.3")])]}),"instanceName":"10"});
            var Q53;
            Q53=makeQuery(id+"F24.opPattern","COPY",BODY,{"derivedFrom":makeQuery(id+"F22.opExtrude","SWEPT_BODY",BODY,{"disambiguationData":[OSD([sQuery(id+"F21.wireOp",EDGE,"E22.0.2.0"),sQuery(id+"F21.wireOp",EDGE,"E22.0.2.1"),sQuery(id+"F21.wireOp",EDGE,"E22.0.2.2"),sQuery(id+"F21.wireOp",EDGE,"E22.0.2.3")])]}),"instanceName":"10"});
            var Q54;
            Q54=makeQuery(id+"F24.opPattern","COPY",BODY,{"derivedFrom":makeQuery(id+"F22.opExtrude","SWEPT_BODY",BODY,{"disambiguationData":[OSD([sQuery(id+"F21.wireOp",EDGE,"E22.0.3.0"),sQuery(id+"F21.wireOp",EDGE,"E22.0.3.1"),sQuery(id+"F21.wireOp",EDGE,"E22.0.3.2"),sQuery(id+"F21.wireOp",EDGE,"E22.0.3.3")])]}),"instanceName":"10"});
            var Q55;
            Q55=makeQuery(id+"F24.opPattern","COPY",BODY,{"derivedFrom":makeQuery(id+"F22.opExtrude","SWEPT_BODY",BODY,{"disambiguationData":[OSD([sQuery(id+"F21.wireOp",EDGE,"E22.0.4.0"),sQuery(id+"F21.wireOp",EDGE,"E22.0.4.1"),sQuery(id+"F21.wireOp",EDGE,"E22.0.4.2"),sQuery(id+"F21.wireOp",EDGE,"E22.0.4.3")])]}),"instanceName":"10"});
            var Q56;
            Q56=makeQuery(id+"F24.opPattern","COPY",BODY,{"derivedFrom":makeQuery(id+"F22.opExtrude","SWEPT_BODY",BODY,{"disambiguationData":[OSD([sQuery(id+"F21.wireOp",EDGE,"E18"),sQuery(id+"F21.wireOp",EDGE,"E19"),sQuery(id+"F21.wireOp",EDGE,"E20"),sQuery(id+"F21.wireOp",EDGE,"E21")])]}),"instanceName":"11"});
            var Q57;
            Q57=makeQuery(id+"F24.opPattern","COPY",BODY,{"derivedFrom":makeQuery(id+"F22.opExtrude","SWEPT_BODY",BODY,{"disambiguationData":[OSD([sQuery(id+"F21.wireOp",EDGE,"E22.0.1.0"),sQuery(id+"F21.wireOp",EDGE,"E22.0.1.1"),sQuery(id+"F21.wireOp",EDGE,"E22.0.1.2"),sQuery(id+"F21.wireOp",EDGE,"E22.0.1.3")])]}),"instanceName":"11"});
            var Q58;
            Q58=makeQuery(id+"F24.opPattern","COPY",BODY,{"derivedFrom":makeQuery(id+"F22.opExtrude","SWEPT_BODY",BODY,{"disambiguationData":[OSD([sQuery(id+"F21.wireOp",EDGE,"E22.0.2.0"),sQuery(id+"F21.wireOp",EDGE,"E22.0.2.1"),sQuery(id+"F21.wireOp",EDGE,"E22.0.2.2"),sQuery(id+"F21.wireOp",EDGE,"E22.0.2.3")])]}),"instanceName":"11"});
            var Q59;
            Q59=makeQuery(id+"F24.opPattern","COPY",BODY,{"derivedFrom":makeQuery(id+"F22.opExtrude","SWEPT_BODY",BODY,{"disambiguationData":[OSD([sQuery(id+"F21.wireOp",EDGE,"E22.0.3.0"),sQuery(id+"F21.wireOp",EDGE,"E22.0.3.1"),sQuery(id+"F21.wireOp",EDGE,"E22.0.3.2"),sQuery(id+"F21.wireOp",EDGE,"E22.0.3.3")])]}),"instanceName":"11"});
            var Q60;
            Q60=makeQuery(id+"F4.opLoft","SWEPT_BODY",BODY,{"disambiguationData":[OSD([makeQuery(id+"F1.imprint","IMPRINT",FACE,{"disambiguationData":[TD([[makeQuery(id+"F1.imprint","IMPRINT",EDGE,{"derivedFrom":sQuery(id+"F1.wireOp",EDGE,"E0")}),1.0]])]}),makeQuery(id+"F3.imprint","IMPRINT",FACE,{"disambiguationData":[TD([[makeQuery(id+"F3.imprint","IMPRINT",EDGE,{"derivedFrom":sQuery(id+"F3.wireOp",EDGE,"E1")}),1.0]])]})])]});
            booleanBodies(context, id + "F25", {"operationType" : BooleanOperationType.SUBTRACTION, "tools" : qUnion([Q0, Q1, Q2, Q3, Q4, Q5, Q6, Q7, Q8, Q9, Q10, Q11, Q12, Q13, Q14, Q15, Q16, Q17, Q18, Q19, Q20, Q21, Q22, Q23, Q24, Q25, Q26, Q27, Q28, Q29, Q30, Q31, Q32, Q33, Q34, Q35, Q36, Q37, Q38, Q39, Q40, Q41, Q42, Q43, Q44, Q45, Q46, Q47, Q48, Q49, Q50, Q51, Q52, Q53, Q54, Q55, Q56, Q57, Q58, Q59]), "targets" : qUnion([Q60])});
        }
    });
